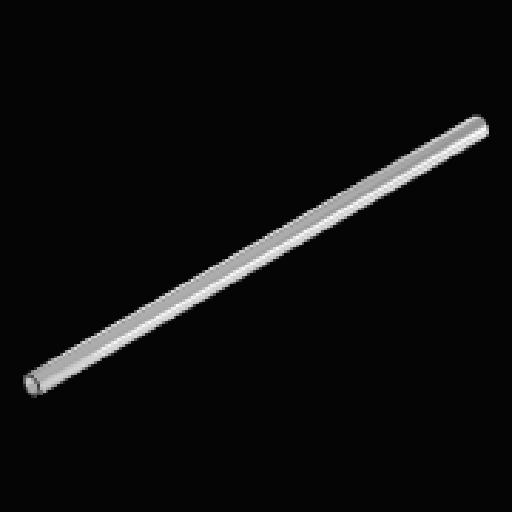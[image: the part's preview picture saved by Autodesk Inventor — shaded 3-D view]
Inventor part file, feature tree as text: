
AUTODESK INVENTOR PART (.ipt)
format: ipt  version: 2023.2 (Build 272271030, 271C)  size: 109,568 bytes
history: native  units: mm
features: extrude x1, sketch x1
ambient origin geometry x8: Origin, YZ Plane, XZ Plane, XY Plane, X Axis, Y Axis, Z Axis, Center Point
bodies: Solid1 (feature_tree)
feature tree (2):
  extrude  "Extrusion1"  Depth=101.0mm TaperAngle=0.0deg
  sketch  "Sketch1"  dims[d0=3.96875mm d1=101.0mm d2=0.0mm d3=0.3556mm]
